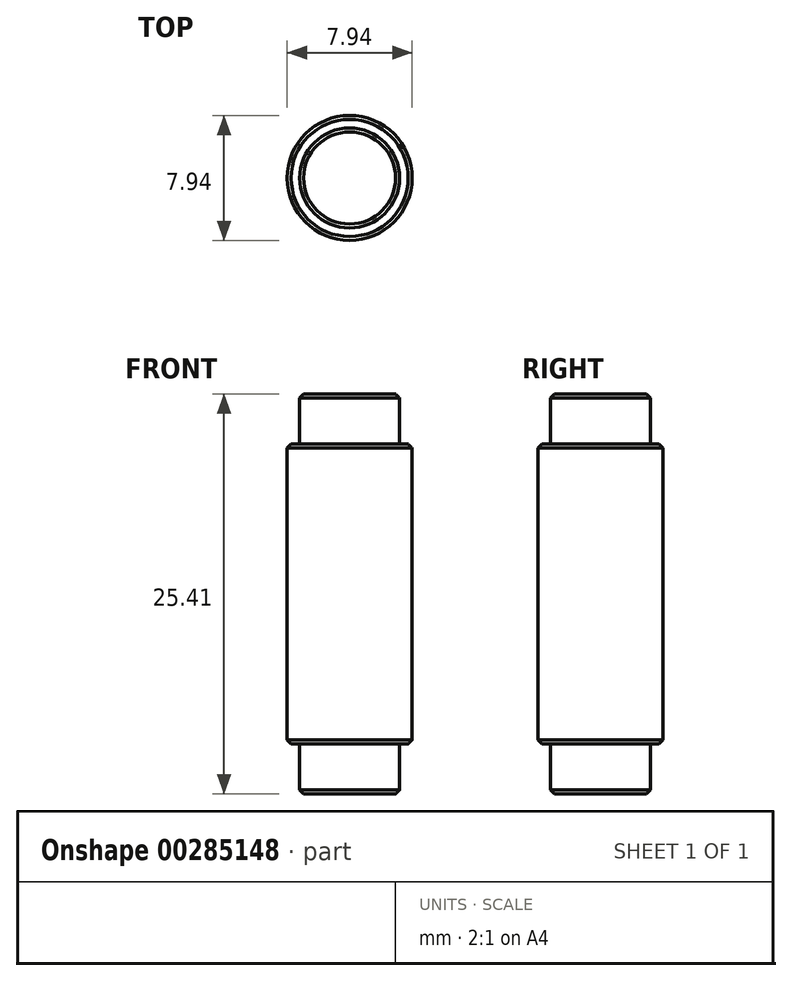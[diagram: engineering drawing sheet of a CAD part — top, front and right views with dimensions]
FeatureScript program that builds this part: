
annotation { "Feature Type Name" : "Feature", "Feature Type Description" : "" }
export const myFeature = defineFeature(function(context is Context, id is Id, definition is map)
    precondition{}
    {
        {
            var Q0;
            Q0=qCreatedBy(makeId("Top.planeOp"),FACE);
            var sketch = newSketch(context, id + "F0", { "sketchPlane" : qUnion([Q0])});
            skCircle(sketch, "E0", {"center": v(0, 0) * mm, "radius": 3.18 * mm});
            skCircle(sketch, "E1", {"center": v(0, 0) * mm, "radius": 3.97 * mm});
            skSolve(sketch);
        }
        {
            var Q0;
            Q0=makeQuery(id+"F0.imprint","IMPRINT",FACE,{"disambiguationData":[TD([[makeQuery(id+"F0.imprint","IMPRINT",EDGE,{"derivedFrom":sQuery(id+"F0.wireOp",EDGE,"E0")}),1.0]])]});
            extrude(context, id + "F1", {"entities" : qUnion([Q0]), "depth" : 3.17 * mm});
        }
        {
            var Q0;
            Q0=makeQuery(id+"F1.opExtrude","CAP_FACE",FACE,{"disambiguationData":[OSD([sQuery(id+"F0.wireOp",EDGE,"E0")])],"isStart":true});
            extrude(context, id + "F2", {"entities" : qUnion([Q0]), "operationType" : NewBodyOperationType.ADD, "depth" : 22.22 * mm});
        }
        {
            var Q0;
            Q0=makeQuery(id+"F0.imprint","IMPRINT",FACE,{"disambiguationData":[TD([[makeQuery(id+"F0.imprint","IMPRINT",EDGE,{"derivedFrom":sQuery(id+"F0.wireOp",EDGE,"E0")}),-1.0]])]});
            extrude(context, id + "F3", {"entities" : qUnion([Q0]), "operationType" : NewBodyOperationType.ADD, "oppositeDirection" : true, "depth" : 19.05 * mm});
        }
        {
            var Q0;
            Q0=makeQuery(id+"F1.opExtrude","CAP_EDGE",EDGE,{"disambiguationData":[OSD([sQuery(id+"F0.wireOp",EDGE,"E0")])],"isStart":false});
            chamfer(context, id + "F4", {"entities" : qUnion([Q0]), "width" : 0.25 * mm, "tangentPropagation" : true});
        }
        {
            var Q0;
            Q0=makeQuery(id+"F3.opExtrude","CAP_EDGE",EDGE,{"disambiguationData":[OSD([sQuery(id+"F0.wireOp",EDGE,"E1")])],"isStart":true});
            chamfer(context, id + "F5", {"entities" : qUnion([Q0]), "width" : 0.25 * mm, "tangentPropagation" : true});
        }
        {
            var Q0;
            Q0=makeQuery(id+"F3.opExtrude","CAP_EDGE",EDGE,{"disambiguationData":[OSD([sQuery(id+"F0.wireOp",EDGE,"E1")])],"isStart":false});
            chamfer(context, id + "F6", {"entities" : qUnion([Q0]), "width" : 0.25 * mm, "tangentPropagation" : true});
        }
        {
            var Q0;
            Q0=makeQuery(id+"F2.opExtrude","CAP_EDGE",EDGE,{"disambiguationData":[OSD([sQuery(id+"F0.wireOp",EDGE,"E0")])],"isStart":false});
            chamfer(context, id + "F7", {"entities" : qUnion([Q0]), "width" : 0.25 * mm, "tangentPropagation" : true});
        }
    });
